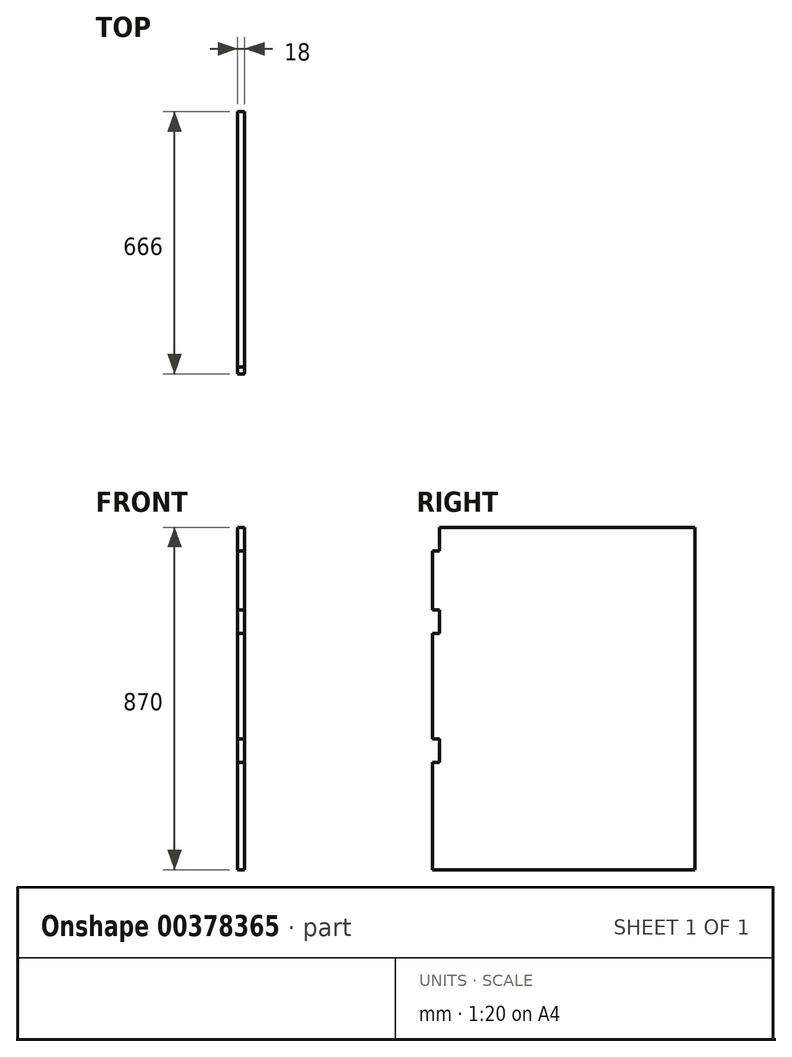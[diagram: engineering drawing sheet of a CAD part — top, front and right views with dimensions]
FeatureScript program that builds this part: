
annotation { "Feature Type Name" : "Feature", "Feature Type Description" : "" }
export const myFeature = defineFeature(function(context is Context, id is Id, definition is map)
    precondition{}
    {
        {
            var Q0;
            Q0=qCreatedBy(makeId("Right.planeOp"),FACE);
            var sketch = newSketch(context, id + "F0", { "sketchPlane" : qUnion([Q0])});
            skLineSegment(sketch, "E0.bottom", {"start": v(333, 435) * mm, "end": v(-333, 435) * mm});
            skLineSegment(sketch, "E0.top", {"start": v(333, -435) * mm, "end": v(-333, -435) * mm});
            skLineSegment(sketch, "E0.left", {"start": v(333, 435) * mm, "end": v(333, -435) * mm});
            skLineSegment(sketch, "E0.right", {"start": v(-333, 435) * mm, "end": v(-333, -435) * mm});
            skPoint(sketch, "E0.middle", {"position": v(0, 0) * mm});
            skSolve(sketch);
        }
        {
            var Q0;
            Q0=qSketchRegion(id+"F0",true);
            extrude(context, id + "F1", {"entities" : qUnion([Q0]), "depth" : 18 * mm});
        }
        {
            var Q0;
            Q0=makeQuery(id+"F1.opExtrude","CAP_FACE",FACE,{"disambiguationData":[OSD([sQuery(id+"F0.wireOp",EDGE,"E0.bottom"),sQuery(id+"F0.wireOp",EDGE,"E0.top"),sQuery(id+"F0.wireOp",EDGE,"E0.left"),sQuery(id+"F0.wireOp",EDGE,"E0.right")])],"isStart":false});
            var sketch = newSketch(context, id + "F2", { "sketchPlane" : qUnion([Q0])});
            skLineSegment(sketch, "E1.bottom", {"start": v(-333, 435) * mm, "end": v(-315, 435) * mm});
            skLineSegment(sketch, "E1.top", {"start": v(-333, 375) * mm, "end": v(-315, 375) * mm});
            skLineSegment(sketch, "E1.left", {"start": v(-333, 435) * mm, "end": v(-333, 375) * mm});
            skLineSegment(sketch, "E1.right", {"start": v(-315, 435) * mm, "end": v(-315, 375) * mm});
            skLineSegment(sketch, "E2.bottom", {"start": v(-333, 225) * mm, "end": v(-315, 225) * mm});
            skLineSegment(sketch, "E2.top", {"start": v(-333, 165) * mm, "end": v(-315, 165) * mm});
            skLineSegment(sketch, "E2.left", {"start": v(-333, 225) * mm, "end": v(-333, 165) * mm});
            skLineSegment(sketch, "E2.right", {"start": v(-315, 225) * mm, "end": v(-315, 165) * mm});
            skLineSegment(sketch, "E3.bottom", {"start": v(-333, -102.5) * mm, "end": v(-315, -102.5) * mm});
            skLineSegment(sketch, "E3.top", {"start": v(-333, -162.5) * mm, "end": v(-315, -162.5) * mm});
            skLineSegment(sketch, "E3.left", {"start": v(-333, -102.5) * mm, "end": v(-333, -162.5) * mm});
            skLineSegment(sketch, "E3.right", {"start": v(-315, -102.5) * mm, "end": v(-315, -162.5) * mm});
            skSolve(sketch);
        }
        {
            var Q0;
            Q0=qSketchRegion(id+"F2",true);
            extrude(context, id + "F3", {"entities" : qUnion([Q0]), "operationType" : NewBodyOperationType.REMOVE, "oppositeDirection" : true, "depth" : 18 * mm});
        }
    });
